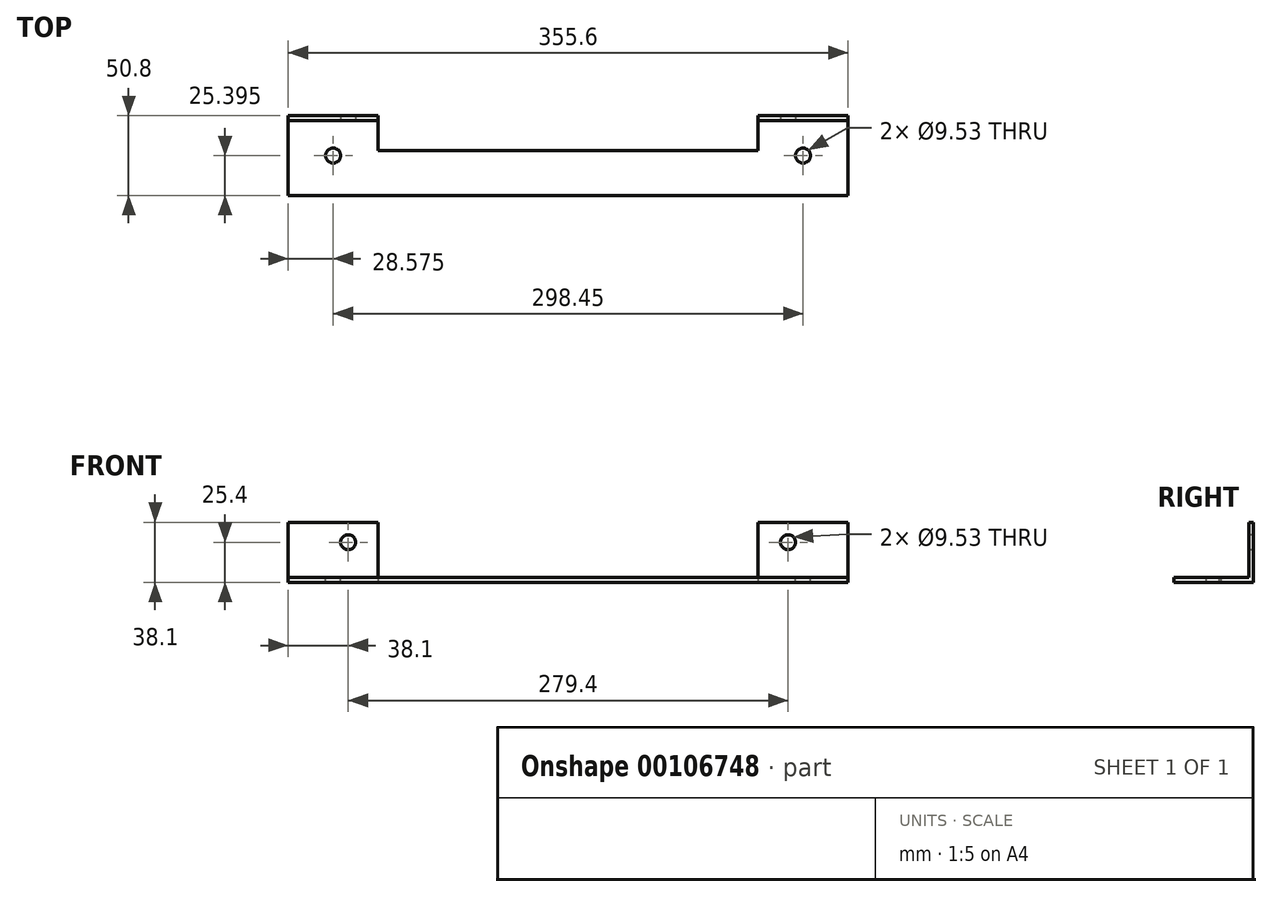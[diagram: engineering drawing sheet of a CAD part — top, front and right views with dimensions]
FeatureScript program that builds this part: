
annotation { "Feature Type Name" : "Feature", "Feature Type Description" : "" }
export const myFeature = defineFeature(function(context is Context, id is Id, definition is map)
    precondition{}
    {
        {
            var Q0;
            Q0=qCreatedBy(makeId("Top.planeOp"),FACE);
            var sketch = newSketch(context, id + "F0", { "sketchPlane" : qUnion([Q0])});
            skLineSegment(sketch, "E0", {"start": v(-120.65, 0) * mm, "end": v(120.65, 0) * mm});
            skLineSegment(sketch, "E1", {"start": v(120.65, 0) * mm, "end": v(120.65, 22.22) * mm});
            skLineSegment(sketch, "E2", {"start": v(120.65, 22.22) * mm, "end": v(177.8, 22.22) * mm});
            skLineSegment(sketch, "E3", {"start": v(177.8, 22.22) * mm, "end": v(177.8, -28.58) * mm});
            skLineSegment(sketch, "E4", {"start": v(177.8, -28.57) * mm, "end": v(-177.8, -28.58) * mm});
            skLineSegment(sketch, "E5", {"start": v(-177.8, -28.58) * mm, "end": v(-177.8, 22.22) * mm});
            skLineSegment(sketch, "E6", {"start": v(-177.8, 22.22) * mm, "end": v(-120.65, 22.22) * mm});
            skLineSegment(sketch, "E7", {"start": v(-120.65, 22.22) * mm, "end": v(-120.65, 0) * mm});
            skLineSegment(sketch, "E8", {"start": v(-177.8, 19.13) * mm, "end": v(-120.65, 19.13) * mm});
            skLineSegment(sketch, "E9", {"start": v(120.65, 19.13) * mm, "end": v(177.8, 19.13) * mm});
            skSolve(sketch);
        }
        {
            var Q0;
            {var subQ5=sQuery(id+"F0.wireOp",EDGE,"E0");Q0=makeQuery(id+"F0.imprint","IMPRINT",FACE,{"disambiguationData":[TD([[makeQuery(id+"F0.imprint","IMPRINT",EDGE,{"derivedFrom":subQ5}),-1.0]])]});}
            extrude(context, id + "F1", {"entities" : qUnion([Q0]), "depth" : 3.1 * mm});
        }
        {
            var Q0;
            {var subQ0=sQuery(id+"F0.wireOp",EDGE,"E6");Q0=makeQuery(id+"F0.imprint","IMPRINT",FACE,{"disambiguationData":[TD([[makeQuery(id+"F0.imprint","IMPRINT",EDGE,{"derivedFrom":subQ0}),-1.0]])]});}
            var Q1;
            {var subQ0=sQuery(id+"F0.wireOp",EDGE,"E2");Q1=makeQuery(id+"F0.imprint","IMPRINT",FACE,{"disambiguationData":[TD([[makeQuery(id+"F0.imprint","IMPRINT",EDGE,{"derivedFrom":subQ0}),-1.0]])]});}
            extrude(context, id + "F2", {"entities" : qUnion([Q0, Q1]), "operationType" : NewBodyOperationType.ADD, "depth" : 38.1 * mm});
        }
        {
            var Q0;
            Q0=makeQuery(id+"F2.opExtrude","SWEPT_FACE",FACE,{"disambiguationData":[OSD([sQuery(id+"F0.wireOp",EDGE,"E9")])]});
            cPlane(context, id + "F3", {"entities" : qUnion([Q0]), "cplaneType" : CPlaneType.OFFSET, "offset" : 0 * mm, "width" : 152.4 * mm, "height" : 152.4 * mm});
        }
        {
            var Q0;
            Q0=qCreatedBy(id+"F3.planeOp",FACE);
            var sketch = newSketch(context, id + "F4", { "sketchPlane" : qUnion([Q0])});
            skLineSegment(sketch, "E10.0", {"start": v(120.65, 38.1) * mm, "end": v(177.8, 38.1) * mm, "construction": true});
            skLineSegment(sketch, "E11.0", {"start": v(-177.8, 38.1) * mm, "end": v(-120.65, 38.1) * mm, "construction": true});
            skLineSegment(sketch, "E12.0", {"start": v(177.8, 38.1) * mm, "end": v(177.8, 3.1) * mm, "construction": true});
            skLineSegment(sketch, "E13.0", {"start": v(-177.8, 38.1) * mm, "end": v(-177.8, 3.1) * mm, "construction": true});
            skPoint(sketch, "E14", {"position": v(-139.7, 25.4) * mm});
            skPoint(sketch, "E15", {"position": v(139.7, 25.4) * mm});
            skSolve(sketch);
        }
        {
            var Q0;
            Q0=sQuery(id+"F4.wireOp",VERTEX,"E14");
            var Q1;
            Q1=sQuery(id+"F4.wireOp",VERTEX,"E15");
            var Q2;
            Q2=makeQuery(id+"F1.opExtrude","SWEPT_BODY",BODY,{"disambiguationData":[OSD([sQuery(id+"F0.wireOp",EDGE,"E0"),sQuery(id+"F0.wireOp",EDGE,"E1"),sQuery(id+"F0.wireOp",EDGE,"E3"),sQuery(id+"F0.wireOp",EDGE,"E4"),sQuery(id+"F0.wireOp",EDGE,"E5"),sQuery(id+"F0.wireOp",EDGE,"E7"),sQuery(id+"F0.wireOp",EDGE,"E8"),sQuery(id+"F0.wireOp",EDGE,"E9")])]});
            hole(context, id + "F5", {"style" : HoleStyle.SIMPLE, "endStyle" : HoleEndStyle.BLIND, "holeDiameter" : 9.52 * mm, "holeDepth" : 12.7 * mm, "startFromSketch" : true, "locations" : qUnion([Q0, Q1]), "scope" : qUnion([Q2])});
        }
        {
            var Q0;
            Q0=makeQuery(id+"F1.opExtrude","CAP_FACE",FACE,{"disambiguationData":[OSD([sQuery(id+"F0.wireOp",EDGE,"E0"),sQuery(id+"F0.wireOp",EDGE,"E1"),sQuery(id+"F0.wireOp",EDGE,"E3"),sQuery(id+"F0.wireOp",EDGE,"E4"),sQuery(id+"F0.wireOp",EDGE,"E5"),sQuery(id+"F0.wireOp",EDGE,"E7"),sQuery(id+"F0.wireOp",EDGE,"E8"),sQuery(id+"F0.wireOp",EDGE,"E9")])],"isStart":false});
            var sketch = newSketch(context, id + "F6", { "sketchPlane" : qUnion([Q0])});
            skLineSegment(sketch, "E16.0", {"start": v(-177.8, -28.58) * mm, "end": v(-177.8, 19.13) * mm, "construction": true});
            skLineSegment(sketch, "E17.0", {"start": v(177.8, 19.13) * mm, "end": v(177.8, -28.57) * mm, "construction": true});
            skPoint(sketch, "E18", {"position": v(-149.23, -3.17) * mm});
            skPoint(sketch, "E19", {"position": v(149.23, -3.17) * mm});
            skLineSegment(sketch, "E20.0", {"start": v(177.8, -28.57) * mm, "end": v(-177.8, -28.58) * mm, "construction": true});
            skSolve(sketch);
        }
        {
            var Q0;
            Q0=sQuery(id+"F6.wireOp",VERTEX,"E18");
            var Q1;
            Q1=sQuery(id+"F6.wireOp",VERTEX,"E19");
            var Q2;
            Q2=makeQuery(id+"F1.opExtrude","SWEPT_BODY",BODY,{"disambiguationData":[OSD([sQuery(id+"F0.wireOp",EDGE,"E0"),sQuery(id+"F0.wireOp",EDGE,"E1"),sQuery(id+"F0.wireOp",EDGE,"E3"),sQuery(id+"F0.wireOp",EDGE,"E4"),sQuery(id+"F0.wireOp",EDGE,"E5"),sQuery(id+"F0.wireOp",EDGE,"E7"),sQuery(id+"F0.wireOp",EDGE,"E8"),sQuery(id+"F0.wireOp",EDGE,"E9")])]});
            hole(context, id + "F7", {"style" : HoleStyle.SIMPLE, "endStyle" : HoleEndStyle.BLIND, "holeDiameter" : 9.52 * mm, "holeDepth" : 12.7 * mm, "startFromSketch" : true, "locations" : qUnion([Q0, Q1]), "scope" : qUnion([Q2])});
        }
    });
